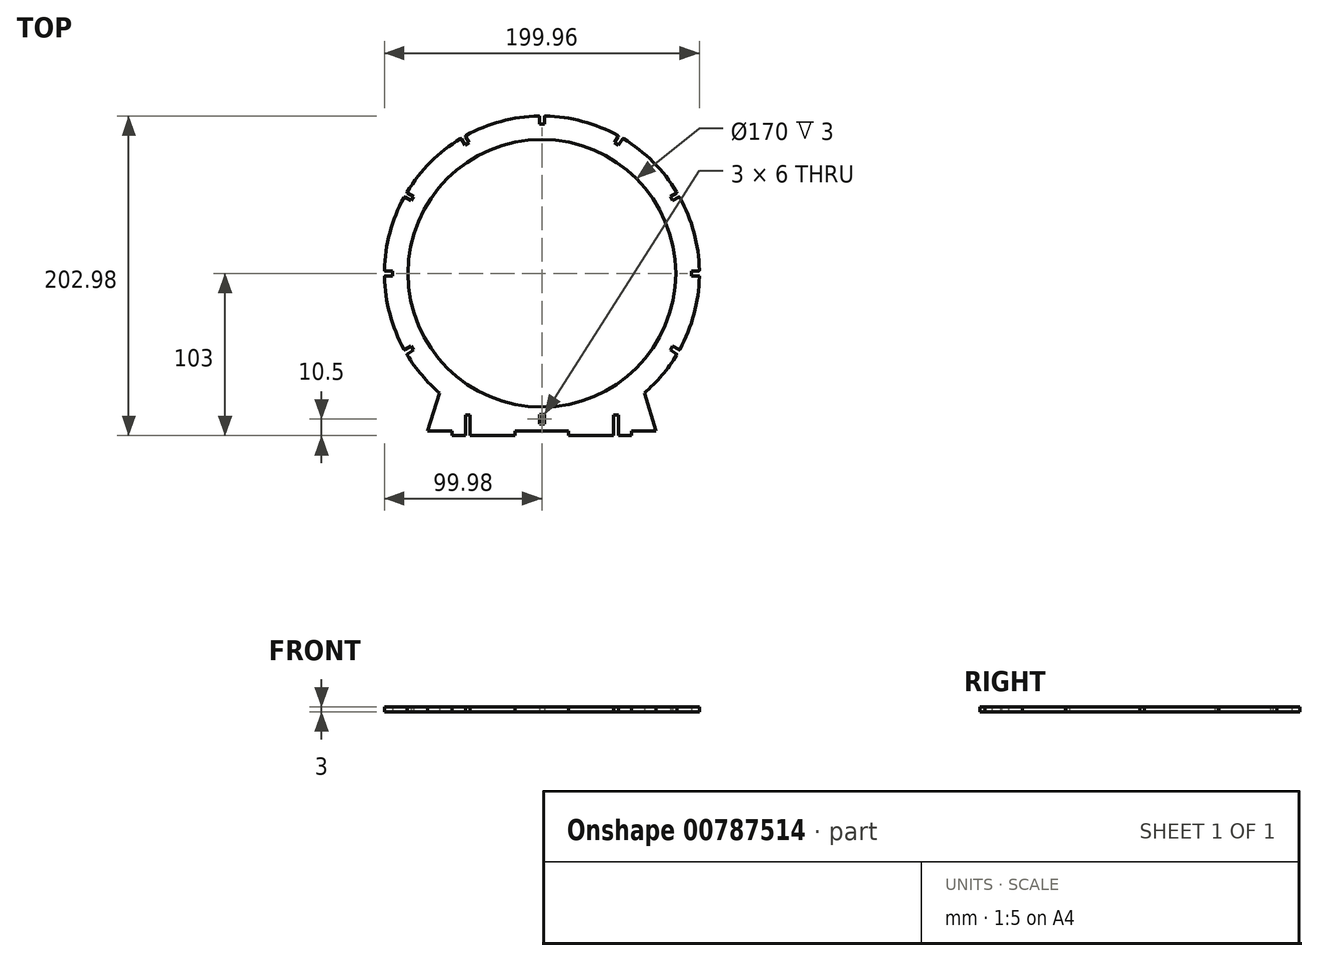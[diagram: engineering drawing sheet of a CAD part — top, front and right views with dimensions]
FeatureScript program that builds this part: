
annotation { "Feature Type Name" : "Feature", "Feature Type Description" : "" }
export const myFeature = defineFeature(function(context is Context, id is Id, definition is map)
    precondition{}
    {
        {
            var Q0;
            Q0=qCreatedBy(makeId("Top.planeOp"),FACE);
            var sketch = newSketch(context, id + "F0", { "sketchPlane" : qUnion([Q0])});
            skCircle(sketch, "E0", {"center": v(0, 0) * mm, "radius": 85 * mm});
            skArc(sketch, "E1", {"start": v(-2.01, 99.98) * mm, "mid": v(-25.88, 96.6) * mm, "end": v(-48.25, 87.6) * mm});
            skLineSegment(sketch, "E2", {"start": v(0, 0) * mm, "end": v(0, -115.1) * mm, "construction": true});
            skLineSegment(sketch, "E3.0", {"start": v(-57, -100) * mm, "end": v(-57, -103) * mm});
            skLineSegment(sketch, "E4.0", {"start": v(57, -100) * mm, "end": v(57, -103) * mm});
            skLineSegment(sketch, "E5.0", {"start": v(1.5, 94.99) * mm, "end": v(1.5, 99.48) * mm});
            skLineSegment(sketch, "E6.0", {"start": v(-1.5, 94.99) * mm, "end": v(-1.5, 99.48) * mm});
            skLineSegment(sketch, "E7.0", {"start": v(1.5, 94.99) * mm, "end": v(-1.5, 94.99) * mm});
            skArc(sketch, "E8.filletArc", {"start": v(-1.5, 99.48) * mm, "mid": v(-1.65, 99.84) * mm, "end": v(-2.01, 99.98) * mm});
            skArc(sketch, "E9.filletArc", {"start": v(2.01, 99.98) * mm, "mid": v(1.65, 99.84) * mm, "end": v(1.5, 99.48) * mm});
            skLineSegment(sketch, "E10.1.0", {"start": v(-46.2, 83.01) * mm, "end": v(-48.44, 86.9) * mm});
            skLineSegment(sketch, "E10.1.1", {"start": v(-48.8, 81.51) * mm, "end": v(-51.04, 85.4) * mm});
            skLineSegment(sketch, "E10.1.2", {"start": v(-46.2, 83.01) * mm, "end": v(-48.8, 81.51) * mm});
            skArc(sketch, "E10.1.3", {"start": v(-51.04, 85.4) * mm, "mid": v(-51.35, 85.64) * mm, "end": v(-51.73, 85.58) * mm});
            skArc(sketch, "E10.1.4", {"start": v(-48.25, 87.6) * mm, "mid": v(-48.49, 87.29) * mm, "end": v(-48.44, 86.9) * mm});
            skLineSegment(sketch, "E10.2.0", {"start": v(-81.51, 48.8) * mm, "end": v(-85.4, 51.04) * mm});
            skLineSegment(sketch, "E10.2.1", {"start": v(-83.01, 46.2) * mm, "end": v(-86.9, 48.44) * mm});
            skLineSegment(sketch, "E10.2.2", {"start": v(-81.51, 48.8) * mm, "end": v(-83.01, 46.2) * mm});
            skArc(sketch, "E10.2.3", {"start": v(-86.9, 48.44) * mm, "mid": v(-87.29, 48.49) * mm, "end": v(-87.6, 48.25) * mm});
            skArc(sketch, "E10.2.4", {"start": v(-85.58, 51.73) * mm, "mid": v(-85.64, 51.35) * mm, "end": v(-85.4, 51.04) * mm});
            skLineSegment(sketch, "E10.3.0", {"start": v(-94.99, 1.5) * mm, "end": v(-99.48, 1.5) * mm});
            skLineSegment(sketch, "E10.3.1", {"start": v(-94.99, -1.5) * mm, "end": v(-99.48, -1.5) * mm});
            skLineSegment(sketch, "E10.3.2", {"start": v(-94.99, 1.5) * mm, "end": v(-94.99, -1.5) * mm});
            skArc(sketch, "E10.3.3", {"start": v(-99.48, -1.5) * mm, "mid": v(-99.84, -1.65) * mm, "end": v(-99.98, -2.01) * mm});
            skArc(sketch, "E10.3.4", {"start": v(-99.98, 2.01) * mm, "mid": v(-99.84, 1.65) * mm, "end": v(-99.48, 1.5) * mm});
            skLineSegment(sketch, "E10.4.0", {"start": v(-83.01, -46.2) * mm, "end": v(-86.9, -48.44) * mm});
            skLineSegment(sketch, "E10.4.1", {"start": v(-81.51, -48.8) * mm, "end": v(-85.4, -51.04) * mm});
            skLineSegment(sketch, "E10.4.2", {"start": v(-83.01, -46.2) * mm, "end": v(-81.51, -48.8) * mm});
            skArc(sketch, "E10.4.3", {"start": v(-85.4, -51.04) * mm, "mid": v(-85.64, -51.35) * mm, "end": v(-85.58, -51.73) * mm});
            skArc(sketch, "E10.4.4", {"start": v(-87.6, -48.25) * mm, "mid": v(-87.29, -48.49) * mm, "end": v(-86.9, -48.44) * mm});
            skLineSegment(sketch, "E10.8.0", {"start": v(81.51, -48.8) * mm, "end": v(85.4, -51.04) * mm});
            skLineSegment(sketch, "E10.8.1", {"start": v(83.01, -46.2) * mm, "end": v(86.9, -48.44) * mm});
            skLineSegment(sketch, "E10.8.2", {"start": v(81.51, -48.8) * mm, "end": v(83.01, -46.2) * mm});
            skArc(sketch, "E10.8.3", {"start": v(86.9, -48.44) * mm, "mid": v(87.29, -48.49) * mm, "end": v(87.6, -48.25) * mm});
            skArc(sketch, "E10.8.4", {"start": v(85.58, -51.73) * mm, "mid": v(85.64, -51.35) * mm, "end": v(85.4, -51.04) * mm});
            skLineSegment(sketch, "E10.9.0", {"start": v(94.99, -1.5) * mm, "end": v(99.48, -1.5) * mm});
            skLineSegment(sketch, "E10.9.1", {"start": v(94.99, 1.5) * mm, "end": v(99.48, 1.5) * mm});
            skLineSegment(sketch, "E10.9.2", {"start": v(94.99, -1.5) * mm, "end": v(94.99, 1.5) * mm});
            skArc(sketch, "E10.9.3", {"start": v(99.48, 1.5) * mm, "mid": v(99.84, 1.65) * mm, "end": v(99.98, 2.01) * mm});
            skArc(sketch, "E10.9.4", {"start": v(99.98, -2.01) * mm, "mid": v(99.84, -1.65) * mm, "end": v(99.48, -1.5) * mm});
            skLineSegment(sketch, "E10.10.0", {"start": v(83.01, 46.2) * mm, "end": v(86.9, 48.44) * mm});
            skLineSegment(sketch, "E10.10.1", {"start": v(81.51, 48.8) * mm, "end": v(85.4, 51.04) * mm});
            skLineSegment(sketch, "E10.10.2", {"start": v(83.01, 46.2) * mm, "end": v(81.51, 48.8) * mm});
            skArc(sketch, "E10.10.3", {"start": v(85.4, 51.04) * mm, "mid": v(85.64, 51.35) * mm, "end": v(85.58, 51.73) * mm});
            skArc(sketch, "E10.10.4", {"start": v(87.6, 48.25) * mm, "mid": v(87.29, 48.49) * mm, "end": v(86.9, 48.44) * mm});
            skLineSegment(sketch, "E10.11.0", {"start": v(48.8, 81.51) * mm, "end": v(51.04, 85.4) * mm});
            skLineSegment(sketch, "E10.11.1", {"start": v(46.2, 83.01) * mm, "end": v(48.44, 86.9) * mm});
            skLineSegment(sketch, "E10.11.2", {"start": v(48.8, 81.51) * mm, "end": v(46.2, 83.01) * mm});
            skArc(sketch, "E10.11.3", {"start": v(48.44, 86.9) * mm, "mid": v(48.49, 87.29) * mm, "end": v(48.25, 87.6) * mm});
            skArc(sketch, "E10.11.4", {"start": v(51.73, 85.58) * mm, "mid": v(51.35, 85.64) * mm, "end": v(51.04, 85.4) * mm});
            skArc(sketch, "E11.trimOffspring", {"start": v(-51.73, 85.58) * mm, "mid": v(-70.71, 70.71) * mm, "end": v(-85.58, 51.73) * mm});
            skArc(sketch, "E12.trimOffspring", {"start": v(-87.6, 48.25) * mm, "mid": v(-96.6, 25.88) * mm, "end": v(-99.98, 2.01) * mm});
            skArc(sketch, "E13.trimOffspring", {"start": v(-99.98, -2.01) * mm, "mid": v(-96.6, -25.88) * mm, "end": v(-87.6, -48.25) * mm});
            skArc(sketch, "E14.trimOffspring", {"start": v(-85.58, -51.73) * mm, "mid": v(-76.26, -64.69) * mm, "end": v(-65, -76) * mm});
            skArc(sketch, "E15.trimOffspring", {"start": v(87.6, -48.25) * mm, "mid": v(96.6, -25.88) * mm, "end": v(99.98, -2.01) * mm});
            skArc(sketch, "E16.trimOffspring", {"start": v(99.98, 2.01) * mm, "mid": v(96.6, 25.88) * mm, "end": v(87.6, 48.25) * mm});
            skArc(sketch, "E17.trimOffspring", {"start": v(85.58, 51.73) * mm, "mid": v(70.71, 70.71) * mm, "end": v(51.73, 85.58) * mm});
            skArc(sketch, "E18.trimOffspring", {"start": v(48.25, 87.6) * mm, "mid": v(25.88, 96.6) * mm, "end": v(2.01, 99.98) * mm});
            skPoint(sketch, "E19", {"position": v(0, -100) * mm});
            skLineSegment(sketch, "E20", {"start": v(-65, -76) * mm, "end": v(-72.5, -100) * mm});
            skLineSegment(sketch, "E21", {"start": v(72.5, -100) * mm, "end": v(65, -76) * mm});
            skLineSegment(sketch, "E22", {"start": v(-57, -103) * mm, "end": v(-48.5, -103) * mm});
            skLineSegment(sketch, "E23", {"start": v(-17, -103) * mm, "end": v(-17, -100) * mm});
            skLineSegment(sketch, "E24", {"start": v(17, -103) * mm, "end": v(17, -100) * mm});
            skLineSegment(sketch, "E25.bottom", {"start": v(-1.5, -89.5) * mm, "end": v(1.5, -89.5) * mm});
            skLineSegment(sketch, "E25.top", {"start": v(-1.5, -95.5) * mm, "end": v(1.5, -95.5) * mm});
            skLineSegment(sketch, "E25.left", {"start": v(-1.5, -89.5) * mm, "end": v(-1.5, -95.5) * mm});
            skLineSegment(sketch, "E25.right", {"start": v(1.5, -89.5) * mm, "end": v(1.5, -95.5) * mm});
            skPoint(sketch, "E25.middle", {"position": v(0, -92.5) * mm});
            skLineSegment(sketch, "E26.trimOffspring", {"start": v(-17, -100) * mm, "end": v(17, -100) * mm});
            skArc(sketch, "E27.trimOffspring", {"start": v(65, -76) * mm, "mid": v(76.26, -64.69) * mm, "end": v(85.58, -51.73) * mm});
            skLineSegment(sketch, "E28", {"start": v(-72.5, -100) * mm, "end": v(-57, -100) * mm});
            skLineSegment(sketch, "E29", {"start": v(57, -100) * mm, "end": v(72.5, -100) * mm});
            skLineSegment(sketch, "E30", {"start": v(-47, -103) * mm, "end": v(-47, -90) * mm, "construction": true});
            skLineSegment(sketch, "E31.bottom", {"start": v(-48.5, -90) * mm, "end": v(-45.5, -90) * mm});
            skLineSegment(sketch, "E31.left", {"start": v(-48.5, -90) * mm, "end": v(-48.5, -103) * mm});
            skLineSegment(sketch, "E31.right", {"start": v(-45.5, -90) * mm, "end": v(-45.5, -103) * mm});
            skPoint(sketch, "E31.middle", {"position": v(-47, -96.5) * mm});
            skLineSegment(sketch, "E32.trimOffspring", {"start": v(-45.5, -103) * mm, "end": v(-17, -103) * mm});
            skLineSegment(sketch, "E33", {"start": v(47, -103) * mm, "end": v(47, -90) * mm, "construction": true});
            skLineSegment(sketch, "E34.trimOffspring", {"start": v(48.5, -103) * mm, "end": v(57, -103) * mm});
            skLineSegment(sketch, "E35", {"start": v(45.5, -103) * mm, "end": v(17, -103) * mm});
            skPoint(sketch, "E36", {"position": v(0, -85) * mm});
            skLineSegment(sketch, "E37.top", {"start": v(45.5, -90) * mm, "end": v(48.5, -90) * mm});
            skLineSegment(sketch, "E37.left", {"start": v(45.5, -103) * mm, "end": v(45.5, -90) * mm});
            skLineSegment(sketch, "E37.right", {"start": v(48.5, -103) * mm, "end": v(48.5, -90) * mm});
            skPoint(sketch, "E37.middle", {"position": v(47, -96.5) * mm});
            skSolve(sketch);
        }
        {
            var Q0;
            Q0=makeQuery(id+"F0.imprint","IMPRINT",FACE,{"disambiguationData":[TD([[makeQuery(id+"F0.imprint","IMPRINT",EDGE,{"derivedFrom":sQuery(id+"F0.wireOp",EDGE,"E0")}),-1.0]])]});
            var Q1;
            {var subQ5=sQuery(id+"F0.wireOp",EDGE,"E20");Q1=makeQuery(id+"F0.imprint","IMPRINT",FACE,{"disambiguationData":[TD([[makeQuery(id+"F0.imprint","IMPRINT",EDGE,{"derivedFrom":subQ5}),1.0]])]});}
            var Q2;
            {var subQ0=sQuery(id+"F0.wireOp",EDGE,"E21");Q2=makeQuery(id+"F0.imprint","IMPRINT",FACE,{"disambiguationData":[TD([[makeQuery(id+"F0.imprint","IMPRINT",EDGE,{"derivedFrom":subQ0}),1.0]])]});}
            var Q3;
            {var subQ0=sQuery(id+"F0.wireOp",EDGE,"E4.0");Q3=makeQuery(id+"F0.imprint","IMPRINT",FACE,{"disambiguationData":[TD([[makeQuery(id+"F0.imprint","IMPRINT",EDGE,{"derivedFrom":subQ0}),-1.0]])]});}
            var Q4;
            {var subQ0=sQuery(id+"F0.wireOp",EDGE,"E3.0");Q4=makeQuery(id+"F0.imprint","IMPRINT",FACE,{"disambiguationData":[TD([[makeQuery(id+"F0.imprint","IMPRINT",EDGE,{"derivedFrom":subQ0}),1.0]])]});}
            extrude(context, id + "F1", {"entities" : qUnion([Q0, Q1, Q2, Q3, Q4]), "depth" : 3 * mm, "offsetDistance" : 25.4 * mm});
        }
    });
